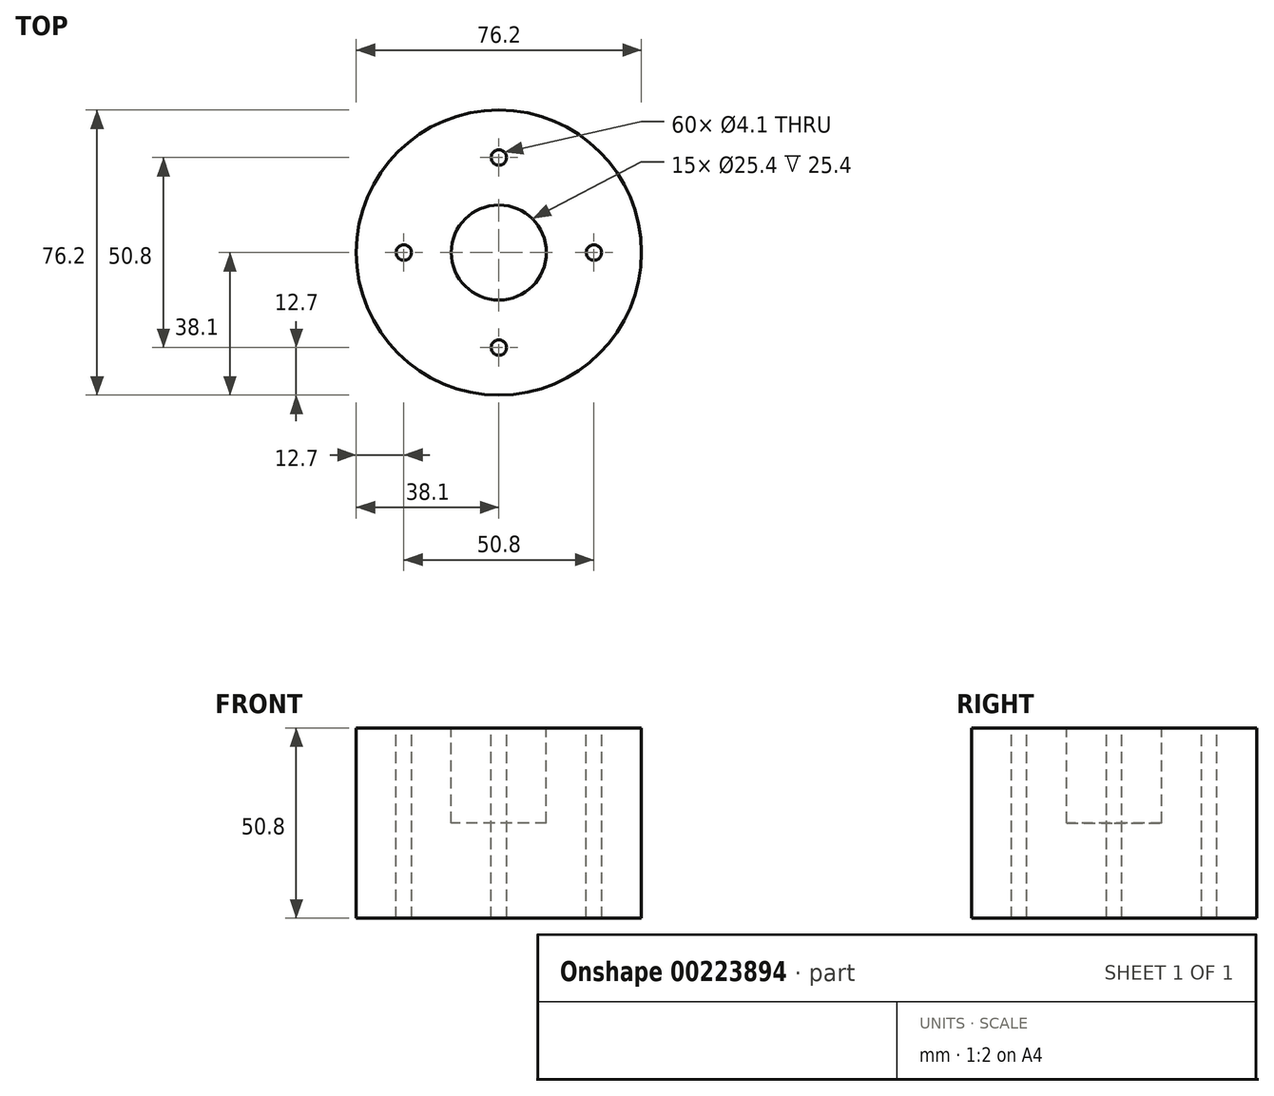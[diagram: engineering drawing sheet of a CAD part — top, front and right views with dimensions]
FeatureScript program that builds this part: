
annotation { "Feature Type Name" : "Feature", "Feature Type Description" : "" }
export const myFeature = defineFeature(function(context is Context, id is Id, definition is map)
    precondition{}
    {
        {
            var Q0;
            Q0=qCreatedBy(makeId("Top.planeOp"),FACE);
            var sketch = newSketch(context, id + "F0", { "sketchPlane" : qUnion([Q0])});
            skCircle(sketch, "E0", {"center": v(0, 0) * mm, "radius": 38.1 * mm});
            skSolve(sketch);
        }
        {
            var Q0;
            Q0 = qSketchRegion(id + "F0", true);
            extrude(context, id + "F1", {"entities" : qUnion([Q0]), "depth" : 50.8 * mm});
        }
        {
            var Q0;
            Q0=makeQuery(id+"F1.opExtrude","CAP_FACE",FACE,{"disambiguationData":[OSD([sQuery(id+"F0.wireOp",EDGE,"E0")])],"isStart":false});
            var sketch = newSketch(context, id + "F2", { "sketchPlane" : qUnion([Q0])});
            skCircle(sketch, "E1", {"center": v(0, 0) * mm, "radius": 12.7 * mm});
            skSolve(sketch);
        }
        {
            var Q0;
            Q0 = qSketchRegion(id + "F2", true);
            extrude(context, id + "F3", {"entities" : qUnion([Q0]), "operationType" : NewBodyOperationType.REMOVE, "oppositeDirection" : true, "depth" : 25.4 * mm});
        }
        {
            var Q0;
            Q0=makeQuery(id+"F1.opExtrude","CAP_FACE",FACE,{"disambiguationData":[OSD([sQuery(id+"F0.wireOp",EDGE,"E0")])],"isStart":false});
            var sketch = newSketch(context, id + "F4", { "sketchPlane" : qUnion([Q0])});
            skPoint(sketch, "E2", {"position": v(-25.4, 0) * mm});
            skPoint(sketch, "E3", {"position": v(0, -25.4) * mm});
            skPoint(sketch, "E4", {"position": v(25.4, 0) * mm});
            skPoint(sketch, "E5", {"position": v(0, 25.4) * mm});
            skCircle(sketch, "E6", {"center": v(0, 0) * mm, "radius": 25.4 * mm});
            skLineSegment(sketch, "E7", {"start": v(0, -25.4) * mm, "end": v(0, 25.4) * mm});
            skLineSegment(sketch, "E8", {"start": v(25.4, 0) * mm, "end": v(-25.4, 0) * mm});
            skSolve(sketch);
        }
        {
            var Q0;
            Q0=sQuery(id+"F4.wireOp",VERTEX,"E4");
            var Q1;
            Q1=sQuery(id+"F4.wireOp",VERTEX,"E5");
            var Q2;
            Q2=sQuery(id+"F4.wireOp",VERTEX,"E2");
            var Q3;
            Q3=sQuery(id+"F4.wireOp",VERTEX,"E3");
            var Q4;
            Q4=makeQuery(id+"F1.opExtrude","SWEPT_BODY",BODY,{"disambiguationData":[OSD([sQuery(id+"F0.wireOp",EDGE,"E0")])]});
            hole(context, id + "F5", {"style" : HoleStyle.SIMPLE, "endStyle" : HoleEndStyle.THROUGH, "standardTappedOrClearance" : lookupTablePath({ "standard" : "ISO", "engagement" : "75%", "pitch" : "0.9 mm", "size" : "M5", "type" : "Tapped" }), "standardBlindInLast" : lookupTablePath({ "standard" : "ISO", "engagement" : "75%", "pitch" : "0.9 mm", "size" : "M5", "type" : "Tapped" }), "holeDiameter" : 4.1 * mm, "locations" : qUnion([Q0, Q1, Q2, Q3]), "scope" : qUnion([Q4]), "isTappedThrough" : true, "showTappedDepth" : true});
        }
    });
